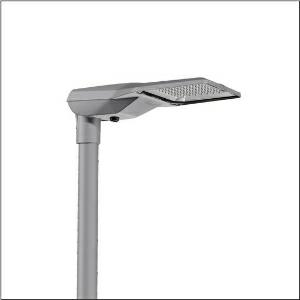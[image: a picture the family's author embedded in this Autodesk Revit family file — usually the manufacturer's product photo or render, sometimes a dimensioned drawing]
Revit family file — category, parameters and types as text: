
# Revit family: streetlight_sl_21_midi___st1_0ab_5xe3m33r08nb_1fb7
name_source: partatom
category: Lighting Fixtures
units: mm (PartAtom-declared; Revit-internal decimal feet)

## family parameters
Cut with Voids When Loaded = No
Host = Face
Light Source = No
Part Type = Normal
Room Calculation Point = No
Round Connector Dimension = Use Diameter
Shared = No

## types (1)
- --- (1 x LED, 19980 lm, 151.2 W, 3000K)
    Apparent Load = 151 VA
    CIE Flux Codes = 40 74 97 100 100
    Color Rendering = 70
    Color Temperature = 3000K
    Default Elevation = 1800 mm
    Description = Streetlight SL 21 midi, mast luminaire, primary light control with lens, of PMMA, primary optical cover: cover, of toughened safety glass, transparent, light distribution: ST1.0aB, light emission: direct distribution, primary light characteristic: asymmetric, installation type: side-entry, post-top, LED, High Power LED, rated luminous flux: 19.980lm, luminous efficacy: 132lm/W, light colour: 730, colour temperature: 3000K, control gear: D4i, control: flexible luminous flux parameterisation, time-dependent luminous flux control, constant luminous flux control, overheat protection, pre-setting: logarithmic dimming characteristic, mains connection: 230..240V, AC, 50/60Hz, start of lifetime: 151W, end of service life: 157W, reduction: 70W, luminaire housing, of diecast aluminium, powder-coated, SITECO metallic grey (DB 702S), corrosivity category C5 high according to DIN EN ISO 12944, please order mast flange separately, inclination adjustable: 0°, 5°, 10°, 15°, sealing non-destructively replaceable, multi-level sealing system, length: 644mm, width: 335mm, height: 110mm, mast flange for spigot size: 42mm (side-entry): 5XC10008XM4, 60/48mm (side-entry/post-top): 5XC10108XM2, 76/60mm (side-entry/post-top): 5XC10108XM1, mounting height: 4..8m, Smart Interface below, protection rating (complete): IP66, insulation class (complete): insulation class II (safety insulation), certification: CE, ENEC, ENEC+, VDE, impact resistance: IK10, permissible operating ambient temperature for outdoor applications: -40..+50°C, standard-compliant lighting for roads and squares, packaging unit: 1 piece

Light Distribution: ST1.0aB
    Height = 111 mm
    Lamp = 1 x LED
    Lamp Light Flux = 19980 lm
    Lamp Power = 151.2 W
    Lamp count = 1
    Length = 644 mm
    Luminous efficacy = 132 lm/W
    Manufacturer = Siteco
    ModVariant = No
    Model = 5XE3M33R08NB
    Number of Poles = 1
    OnlyDefault = Yes
    Power Factor = 1
    Product Name = Streetlight SL 21 midi | ST1.0aB
    Product group = mast luminaire | pylon top
    ProductGroupID = 6100
    Protection Class = Protection class II
    Protection Degree = IP 66
    RLX_Detail_Level = 1
    RLX_Emergency_Light_Flux = 0 lm
    RLX_Emergency_Type = 0
    RLX_Emergency_Type_DB = No
    RlxData = <blob elided: 26993 chars, md5=292b7360>
    Socket = socket
    Standby Power = 0 W
    System Light Flux = 19980 lm
    System Power = 151 W
    Type Comments = factory setting: luminous flux: 100 % | dim-lin: 254 | 802 mA
    Type Image = l_1004300.jpg
    URL = http://relux.com
    VarID = @adj_167661
    Voltage = 0 V
    Weight = 0.00 kg
    Width = 336 mm

## geometry (parser evidence)
native form markers: Blend x4, Sweep x10
no freeform markers — native parametric forms only
